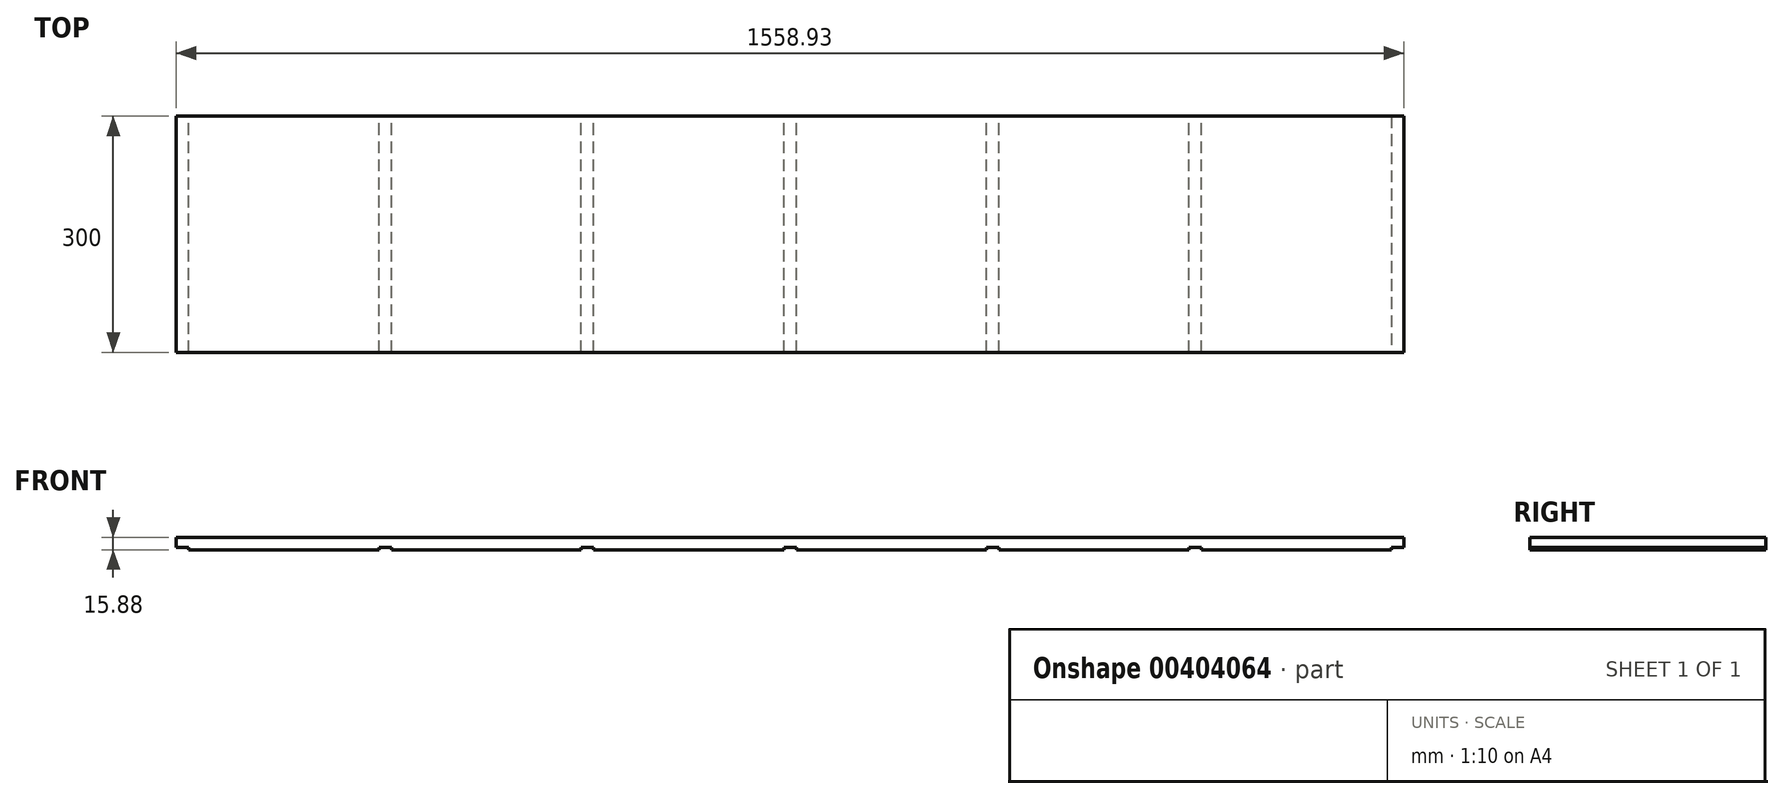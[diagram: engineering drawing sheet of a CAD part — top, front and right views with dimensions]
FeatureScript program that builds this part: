
annotation { "Feature Type Name" : "Feature", "Feature Type Description" : "" }
export const myFeature = defineFeature(function(context is Context, id is Id, definition is map)
    precondition{}
    {
        {
            var Q0;
            Q0=qCreatedBy(makeId("Top.planeOp"),FACE);
            var sketch = newSketch(context, id + "F0", { "sketchPlane" : qUnion([Q0])});
            skLineSegment(sketch, "E0.bottom", {"start": v(-420.76, 150.1) * mm, "end": v(1138.17, 150.1) * mm});
            skLineSegment(sketch, "E0.top", {"start": v(-420.76, -149.9) * mm, "end": v(1138.17, -149.9) * mm});
            skLineSegment(sketch, "E0.left", {"start": v(-420.76, 150.1) * mm, "end": v(-420.76, -149.9) * mm});
            skLineSegment(sketch, "E0.right", {"start": v(1138.17, 150.1) * mm, "end": v(1138.17, -149.9) * mm});
            skSolve(sketch);
        }
        {
            var Q0;
            Q0 = qSketchRegion(id + "F0", true);
            extrude(context, id + "F1", {"entities" : qUnion([Q0]), "depth" : 15.88 * mm});
        }
        {
            var Q0;
            Q0=makeQuery(id+"F1.opExtrude","CAP_FACE",FACE,{"disambiguationData":[OSD([sQuery(id+"F0.wireOp",EDGE,"E0.bottom"),sQuery(id+"F0.wireOp",EDGE,"E0.top"),sQuery(id+"F0.wireOp",EDGE,"E0.left"),sQuery(id+"F0.wireOp",EDGE,"E0.right")])],"isStart":true});
            var sketch = newSketch(context, id + "F2", { "sketchPlane" : qUnion([Q0])});
            skLineSegment(sketch, "E1.bottom", {"start": v(-420.76, 149.9) * mm, "end": v(-404.88, 149.9) * mm});
            skLineSegment(sketch, "E1.top", {"start": v(-420.76, -150.1) * mm, "end": v(-404.88, -150.1) * mm});
            skLineSegment(sketch, "E1.left", {"start": v(-420.76, 149.9) * mm, "end": v(-420.76, -150.1) * mm});
            skLineSegment(sketch, "E1.right", {"start": v(-404.88, 149.9) * mm, "end": v(-404.88, -150.1) * mm});
            skLineSegment(sketch, "E2.bottom", {"start": v(-163.58, 149.9) * mm, "end": v(-147.7, 149.9) * mm});
            skLineSegment(sketch, "E2.top", {"start": v(-163.58, -150.1) * mm, "end": v(-147.7, -150.1) * mm});
            skLineSegment(sketch, "E2.left", {"start": v(-163.58, 149.9) * mm, "end": v(-163.58, -150.1) * mm});
            skLineSegment(sketch, "E2.right", {"start": v(-147.7, 149.9) * mm, "end": v(-147.7, -150.1) * mm});
            skLineSegment(sketch, "E3.bottom", {"start": v(93.6, 149.9) * mm, "end": v(109.47, 149.9) * mm});
            skLineSegment(sketch, "E3.top", {"start": v(93.6, -150.1) * mm, "end": v(109.47, -150.1) * mm});
            skLineSegment(sketch, "E3.left", {"start": v(93.6, 149.9) * mm, "end": v(93.6, -150.1) * mm});
            skLineSegment(sketch, "E3.right", {"start": v(109.47, 149.9) * mm, "end": v(109.47, -150.1) * mm});
            skLineSegment(sketch, "E4.bottom", {"start": v(350.77, 149.9) * mm, "end": v(366.64, 149.9) * mm});
            skLineSegment(sketch, "E4.top", {"start": v(350.77, -150.1) * mm, "end": v(366.64, -150.1) * mm});
            skLineSegment(sketch, "E4.left", {"start": v(350.77, 149.9) * mm, "end": v(350.77, -150.1) * mm});
            skLineSegment(sketch, "E4.right", {"start": v(366.64, 149.9) * mm, "end": v(366.64, -150.1) * mm});
            skLineSegment(sketch, "E5.bottom", {"start": v(607.94, 149.9) * mm, "end": v(623.82, 149.9) * mm});
            skLineSegment(sketch, "E5.top", {"start": v(607.94, -150.1) * mm, "end": v(623.82, -150.1) * mm});
            skLineSegment(sketch, "E5.left", {"start": v(607.94, 149.9) * mm, "end": v(607.94, -150.1) * mm});
            skLineSegment(sketch, "E5.right", {"start": v(623.82, 149.9) * mm, "end": v(623.82, -150.1) * mm});
            skLineSegment(sketch, "E6.top", {"start": v(619.82, -150.1) * mm, "end": v(635.7, -150.1) * mm});
            skLineSegment(sketch, "E7.bottom", {"start": v(865.12, 149.9) * mm, "end": v(881, 149.9) * mm});
            skLineSegment(sketch, "E7.top", {"start": v(865.12, -150.1) * mm, "end": v(881, -150.1) * mm});
            skLineSegment(sketch, "E7.left", {"start": v(865.12, 149.9) * mm, "end": v(865.12, -150.1) * mm});
            skLineSegment(sketch, "E7.right", {"start": v(881, 149.9) * mm, "end": v(881, -150.1) * mm});
            skLineSegment(sketch, "E8.bottom", {"start": v(1138.17, -150.1) * mm, "end": v(1122.3, -150.1) * mm});
            skLineSegment(sketch, "E8.top", {"start": v(1138.17, 149.9) * mm, "end": v(1122.3, 149.9) * mm});
            skLineSegment(sketch, "E8.left", {"start": v(1138.17, -150.1) * mm, "end": v(1138.17, 149.9) * mm});
            skLineSegment(sketch, "E8.right", {"start": v(1122.3, -150.1) * mm, "end": v(1122.3, 149.9) * mm});
            skSolve(sketch);
        }
        {
            var Q0;
            Q0 = qSketchRegion(id + "F2", true);
            extrude(context, id + "F3", {"entities" : qUnion([Q0]), "operationType" : NewBodyOperationType.REMOVE, "oppositeDirection" : true, "depth" : 3.17 * mm});
        }
    });
